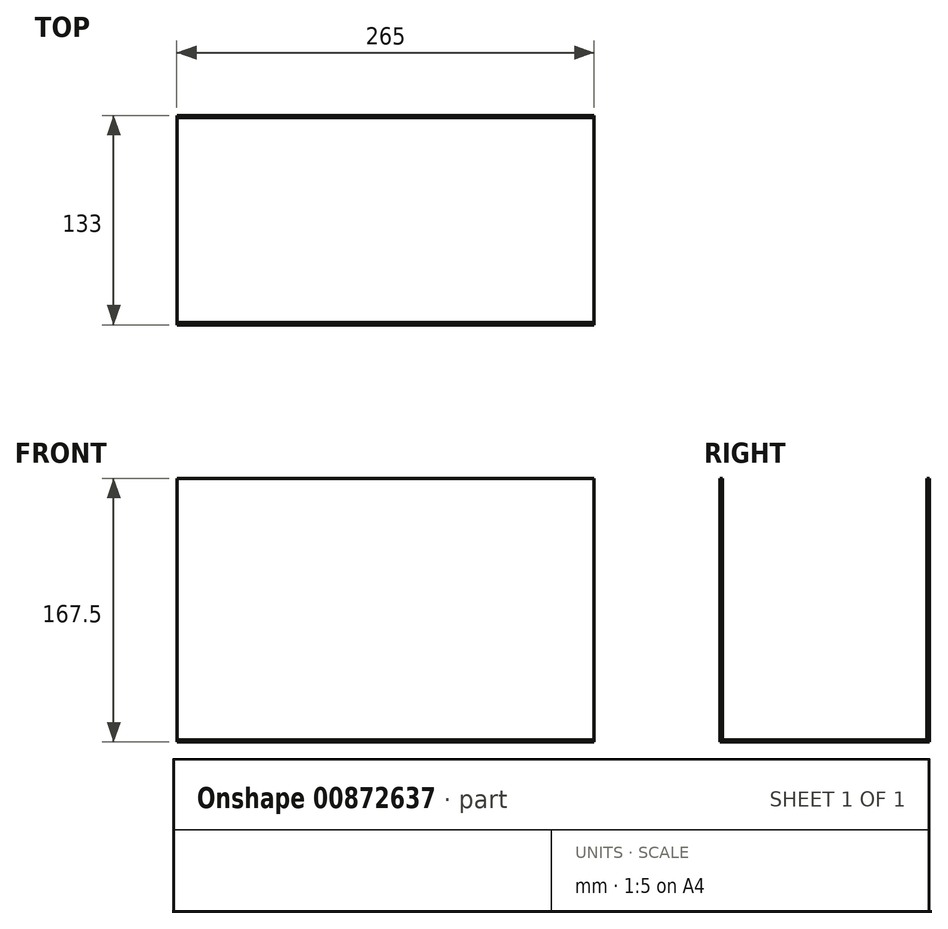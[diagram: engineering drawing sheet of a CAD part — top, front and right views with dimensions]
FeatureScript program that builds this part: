
annotation { "Feature Type Name" : "Feature", "Feature Type Description" : "" }
export const myFeature = defineFeature(function(context is Context, id is Id, definition is map)
    precondition{}
    {
        {
            var Q0;
            Q0=qCreatedBy(makeId("Top.planeOp"),FACE);
            var sketch = newSketch(context, id + "F0", { "sketchPlane" : qUnion([Q0])});
            skLineSegment(sketch, "E0.bottom", {"start": v(-129.8, 26.07) * mm, "end": v(135.2, 26.07) * mm});
            skLineSegment(sketch, "E0.top", {"start": v(-129.8, -103.93) * mm, "end": v(135.2, -103.93) * mm});
            skLineSegment(sketch, "E0.left", {"start": v(-129.8, 26.07) * mm, "end": v(-129.8, -103.93) * mm});
            skLineSegment(sketch, "E0.right", {"start": v(135.2, 26.07) * mm, "end": v(135.2, -103.93) * mm});
            skSolve(sketch);
        }
        {
            var Q0;
            Q0=qCreatedBy(makeId("Top.planeOp"),FACE);
            var sketch = newSketch(context, id + "F1", { "sketchPlane" : qUnion([Q0])});
            skLineSegment(sketch, "E1.bottom", {"start": v(-129.8, -103.93) * mm, "end": v(135.2, -103.93) * mm});
            skLineSegment(sketch, "E1.top", {"start": v(-129.8, -105.43) * mm, "end": v(135.2, -105.43) * mm});
            skLineSegment(sketch, "E1.left", {"start": v(-129.8, -103.93) * mm, "end": v(-129.8, -105.43) * mm});
            skLineSegment(sketch, "E1.right", {"start": v(135.2, -103.93) * mm, "end": v(135.2, -105.43) * mm});
            skSolve(sketch);
        }
        {
            var Q0;
            Q0=qCreatedBy(makeId("Top.planeOp"),FACE);
            var sketch = newSketch(context, id + "F2", { "sketchPlane" : qUnion([Q0])});
            skLineSegment(sketch, "E2.bottom", {"start": v(-129.8, 27.57) * mm, "end": v(135.2, 27.57) * mm});
            skLineSegment(sketch, "E2.top", {"start": v(-129.8, 26.07) * mm, "end": v(135.2, 26.07) * mm});
            skLineSegment(sketch, "E2.left", {"start": v(-129.8, 27.57) * mm, "end": v(-129.8, 26.07) * mm});
            skLineSegment(sketch, "E2.right", {"start": v(135.2, 27.57) * mm, "end": v(135.2, 26.07) * mm});
            skSolve(sketch);
        }
        {
            var Q0;
            Q0=makeQuery(id+"F2.imprint","IMPRINT",FACE,{"disambiguationData":[TD([[makeQuery(id+"F2.imprint","IMPRINT",EDGE,{"derivedFrom":sQuery(id+"F2.wireOp",EDGE,"E2.bottom")}),-1.0]])]});
            var Q1;
            Q1=makeQuery(id+"F0.imprint","IMPRINT",FACE,{"disambiguationData":[TD([[makeQuery(id+"F0.imprint","IMPRINT",EDGE,{"derivedFrom":sQuery(id+"F0.wireOp",EDGE,"E0.bottom")}),-1.0]])]});
            var Q2;
            Q2=makeQuery(id+"F1.imprint","IMPRINT",FACE,{"disambiguationData":[TD([[makeQuery(id+"F1.imprint","IMPRINT",EDGE,{"derivedFrom":sQuery(id+"F1.wireOp",EDGE,"E1.bottom")}),-1.0]])]});
            extrude(context, id + "F3", {"entities" : qUnion([Q0, Q1, Q2]), "depth" : 1.5 * mm, "offsetDistance" : 25 * mm});
        }
        {
            var Q0;
            Q0=makeQuery(id+"F3.opExtrude","CAP_FACE",FACE,{"disambiguationData":[OSD([sQuery(id+"F2.wireOp",EDGE,"E2.bottom"),sQuery(id+"F2.wireOp",EDGE,"E2.top"),sQuery(id+"F2.wireOp",EDGE,"E2.left"),sQuery(id+"F2.wireOp",EDGE,"E2.right")])],"isStart":false});
            var Q1;
            Q1=makeQuery(id+"F3.opExtrude","CAP_FACE",FACE,{"disambiguationData":[OSD([sQuery(id+"F1.wireOp",EDGE,"E1.bottom"),sQuery(id+"F1.wireOp",EDGE,"E1.top"),sQuery(id+"F1.wireOp",EDGE,"E1.left"),sQuery(id+"F1.wireOp",EDGE,"E1.right")])],"isStart":false});
            extrude(context, id + "F4", {"entities" : qUnion([Q0, Q1]), "depth" : 166 * mm, "offsetDistance" : 25 * mm});
        }
    });
